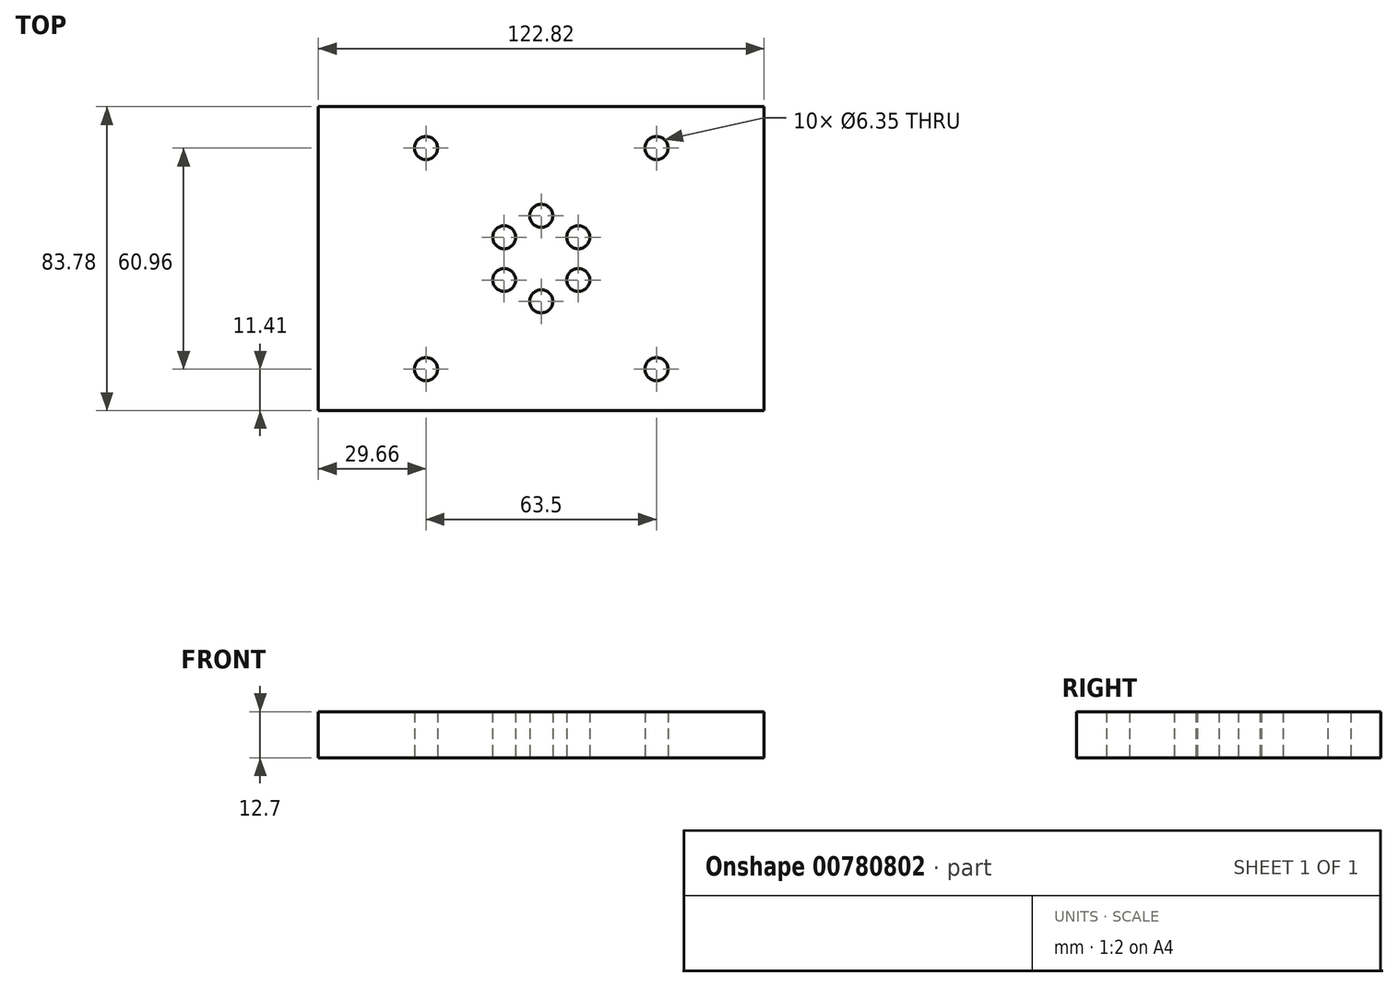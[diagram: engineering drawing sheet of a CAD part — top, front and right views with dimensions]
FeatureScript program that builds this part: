
annotation { "Feature Type Name" : "Feature", "Feature Type Description" : "" }
export const myFeature = defineFeature(function(context is Context, id is Id, definition is map)
    precondition{}
    {
        {
            var Q0;
            Q0=qCreatedBy(makeId("Top.planeOp"),FACE);
            var sketch = newSketch(context, id + "F0", { "sketchPlane" : qUnion([Q0])});
            skLineSegment(sketch, "E0.bottom", {"start": v(61.41, 41.89) * mm, "end": v(-61.41, 41.89) * mm});
            skLineSegment(sketch, "E0.top", {"start": v(61.41, -41.89) * mm, "end": v(-61.41, -41.89) * mm});
            skLineSegment(sketch, "E0.left", {"start": v(61.41, 41.89) * mm, "end": v(61.41, -41.89) * mm});
            skLineSegment(sketch, "E0.right", {"start": v(-61.41, 41.89) * mm, "end": v(-61.41, -41.89) * mm});
            skPoint(sketch, "E0.middle", {"position": v(0, 0) * mm});
            skCircle(sketch, "E1", {"center": v(-31.75, 30.48) * mm, "radius": 3.18 * mm});
            skCircle(sketch, "E2.MirrorC", {"center": v(31.75, 30.48) * mm, "radius": 3.18 * mm});
            skCircle(sketch, "E3.MirrorC", {"center": v(-31.75, -30.48) * mm, "radius": 3.18 * mm});
            skCircle(sketch, "E4.MirrorC", {"center": v(31.75, -30.48) * mm, "radius": 3.18 * mm});
            skCircle(sketch, "E5", {"center": v(0, 0) * mm, "radius": 11.78 * mm, "construction": true});
            skCircle(sketch, "E6", {"center": v(0, 11.78) * mm, "radius": 3.18 * mm});
            skCircle(sketch, "E7.1.1", {"center": v(-10.2, 5.9) * mm, "radius": 3.18 * mm});
            skCircle(sketch, "E7.2.1", {"center": v(-10.2, -5.9) * mm, "radius": 3.18 * mm});
            skCircle(sketch, "E7.3.1", {"center": v(0, -11.78) * mm, "radius": 3.18 * mm});
            skCircle(sketch, "E7.4.1", {"center": v(10.2, -5.9) * mm, "radius": 3.18 * mm});
            skCircle(sketch, "E7.5.1", {"center": v(10.2, 5.9) * mm, "radius": 3.18 * mm});
            skSolve(sketch);
        }
        {
            var Q0;
            Q0 = qSketchRegion(id + "F0", true);
            extrude(context, id + "F1", {"entities" : qUnion([Q0]), "depth" : 12.7 * mm, "offsetDistance" : 25.4 * mm});
        }
    });
